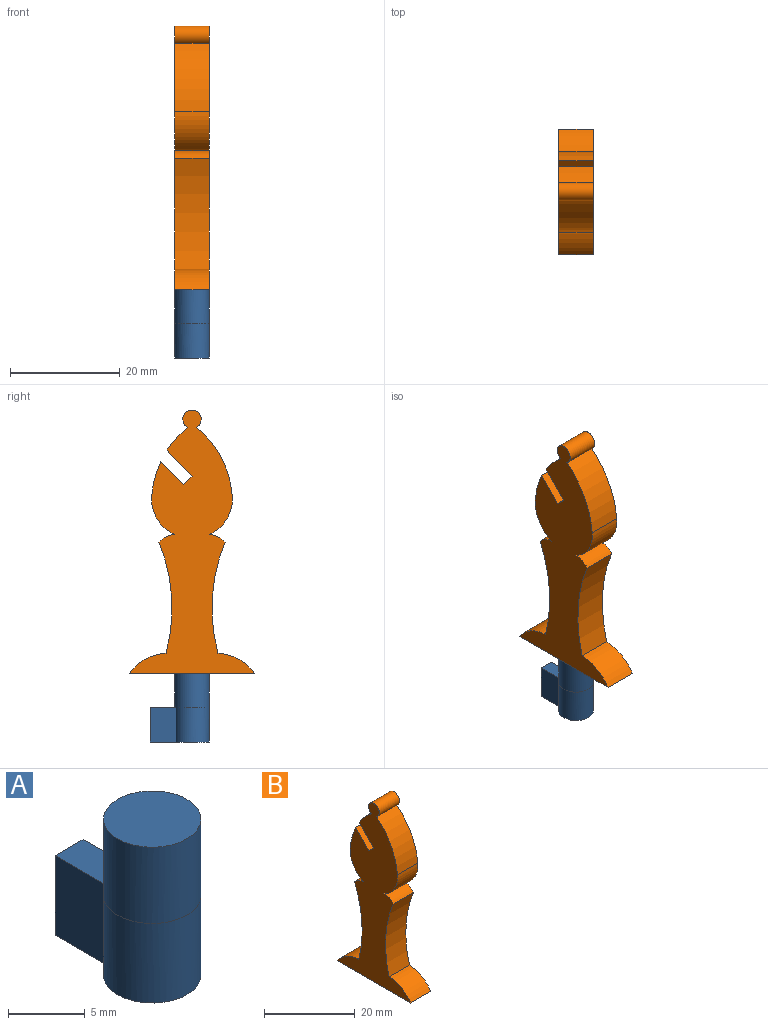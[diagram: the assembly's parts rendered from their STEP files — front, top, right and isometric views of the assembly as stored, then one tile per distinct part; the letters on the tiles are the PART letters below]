
ASSEMBLY  parts=2 mates=1
PART A: 8 faces, bbox 6.4x10.8x12.5 mm
  f0: plane 4.77x2.58mm, normal (0,0,1), area 11.8mm2, adj f1,f2,f4,f6
  f1: plane 6.35x2.58mm, normal (0,1,0), area 16.4mm2, adj f0,f2,f4,f5
  f2: plane 6.35x4.76mm, normal (-1,0,0), area 30.2mm2, adj f0,f1,f3,f5
  f3: cylinder r=3.17mm len=6.35mm, axis (0,0,-1), area 109.8mm2, adj f2,f4,f5,f6
  f4: plane 6.35x4.75mm, normal (1,0,0), area 30.2mm2, adj f0,f1,f3,f5
  f5: plane 10.83x6.35mm, normal (0,0,-1), area 43.5mm2, adj f1,f2,f3,f4
  f6: cylinder r=3.17mm len=6.35mm, axis (0,0,-1), area 121.6mm2, adj f0,f3,f7
  f7: plane 6.35x6.35mm, normal (0,0,1), area 31.7mm2, adj f6
PART B: 18 faces, bbox 6.3x22.9x48.1 mm
  f0: plane 48.11x22.86mm, normal (-1,0,0), area 469.6mm2, adj f2,f3,f4,f5,f6,f7,f8,f9
  f1: plane 48.11x22.86mm, normal (1,0,0), area 469.6mm2, adj f2,f3,f4,f5,f6,f7,f8,f9
  f2: cylinder r=17.78mm len=6.32mm, axis (-1,0,0), area 35.5mm2, adj f0,f1,f8,f9
  f3: cylinder r=17.78mm len=12.45mm, axis (-1,0,0), area 91.4mm2, adj f0,f1,f6,f8
  f4: cylinder r=17.78mm len=6.32mm, axis (-1,0,0), area 41.2mm2, adj f0,f1,f7,f11
  f5: plane 22.86x6.32mm, normal (0,0,-1), area 144.6mm2, adj f0,f1,f13,f15
  f6: cylinder r=7.06mm len=7.13mm, axis (-1,0,0), area 56mm2, adj f0,f1,f3,f17
  f7: cylinder r=7.06mm len=7.13mm, axis (-1,0,0), area 56mm2, adj f0,f1,f4,f14
  f8: cylinder r=1.67mm len=6.32mm, axis (-1,0,0), area 55.8mm2, adj f0,f1,f2,f3
  f9: plane 6.32x4.75mm, normal (0,0.72,-0.69), area 41.6mm2, adj f0,f1,f2,f10
  f10: plane 6.32x1.6mm, normal (0,0.69,0.72), area 14mm2, adj f0,f1,f9,f11
  f11: plane 6.32x4.26mm, normal (0,-0.72,0.69), area 37.3mm2, adj f0,f1,f4,f10
  f12: cylinder r=31.27mm len=20.24mm, axis (1,0,0), area 130.6mm2, adj f0,f1,f13,f14
  f13: cylinder r=8.61mm len=6.69mm, axis (1,0,0), area 50.3mm2, adj f0,f1,f5,f12
  f14: cylinder r=3.69mm len=6.32mm, axis (1,0,0), area 21.2mm2, adj f0,f1,f7,f12
  f15: cylinder r=8.61mm len=6.69mm, axis (1,0,0), area 50.3mm2, adj f0,f1,f5,f16
  f16: cylinder r=31.27mm len=20.24mm, axis (1,0,0), area 130.6mm2, adj f0,f1,f15,f17
  f17: cylinder r=3.69mm len=6.32mm, axis (1,0,0), area 21.2mm2, adj f0,f1,f6,f16
PLACE A at identity
PLACE B t=(0,0,25.15)mm
MATE fastened B.f5 <-> A.f6  axis (0,0,-1) through (0,0,12.45)mm
